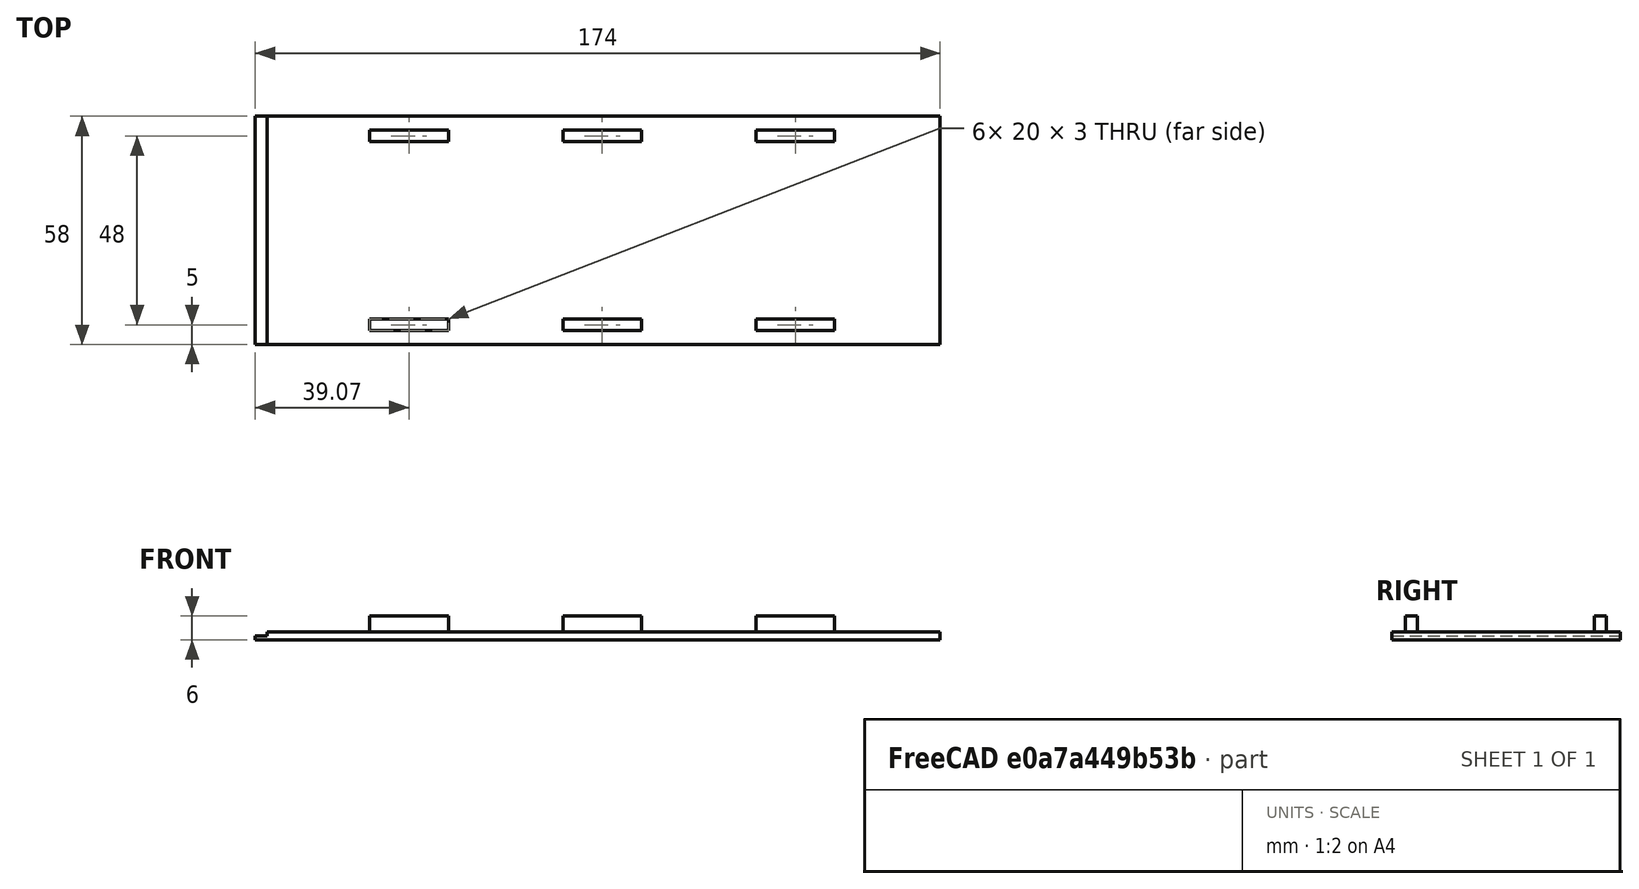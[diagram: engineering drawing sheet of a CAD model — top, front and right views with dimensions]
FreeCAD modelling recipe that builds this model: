
FCSTD DOCUMENT  (FreeCAD 0.21R33694 (Git))
Label: maze_cover_A
License: All rights reserved
LicenseURL: https://en.wikipedia.org/wiki/All_rights_reserved
objects: Part::Box×8, Part::MultiFuse×1
note: 9 computed .brp shape members not serialized (recipe doc carries the construction recipe); baked Part::Feature solids carry a one-line shape summary decoded from their .brp

FEATURE [Part::Box] Box  label="Cube"
  AttacherType = Attacher::AttachEngine3D
  Height = 2
  Length = 171
  Placement = pos=(3,0,0) rot=(0,0,1;0rad)
  Width = 58
FEATURE [Part::Box] Box001  label="Cube001"
  AttacherType = Attacher::AttachEngine3D
  Height = 6
  Length = 20
  Placement = pos=(29.07,3.5,0) rot=(0,0,1;0rad)
  Width = 3
FEATURE [Part::Box] Box002  label="Cube002"
  AttacherType = Attacher::AttachEngine3D
  Height = 6
  Length = 20
  Placement = pos=(78.15,3.5,0) rot=(0,0,1;0rad)
  Width = 3
FEATURE [Part::Box] Box003  label="Cube003"
  AttacherType = Attacher::AttachEngine3D
  Height = 6
  Length = 20
  Placement = pos=(127.22,3.5,0) rot=(0,0,1;0rad)
  Width = 3
FEATURE [Part::Box] Box004  label="Cube004"
  AttacherType = Attacher::AttachEngine3D
  Height = 6
  Length = 20
  Placement = pos=(29.07,51.5,0) rot=(0,0,1;0rad)
  Width = 3
FEATURE [Part::Box] Box005  label="Cube005"
  AttacherType = Attacher::AttachEngine3D
  Height = 6
  Length = 20
  Placement = pos=(78.15,51.5,0) rot=(0,0,1;0rad)
  Width = 3
FEATURE [Part::Box] Box006  label="Cube006"
  AttacherType = Attacher::AttachEngine3D
  Height = 6
  Length = 20
  Placement = pos=(127.22,51.5,0) rot=(0,0,1;0rad)
  Width = 3
FEATURE [Part::Box] Box007  label="Cube007"
  AttacherType = Attacher::AttachEngine3D
  Height = 1
  Length = 3
  Width = 58
FEATURE [Part::MultiFuse] Fusion
  Shapes = -> [Box007,Box006,Box005,Box004,Box003,Box002,Box001,Box]
